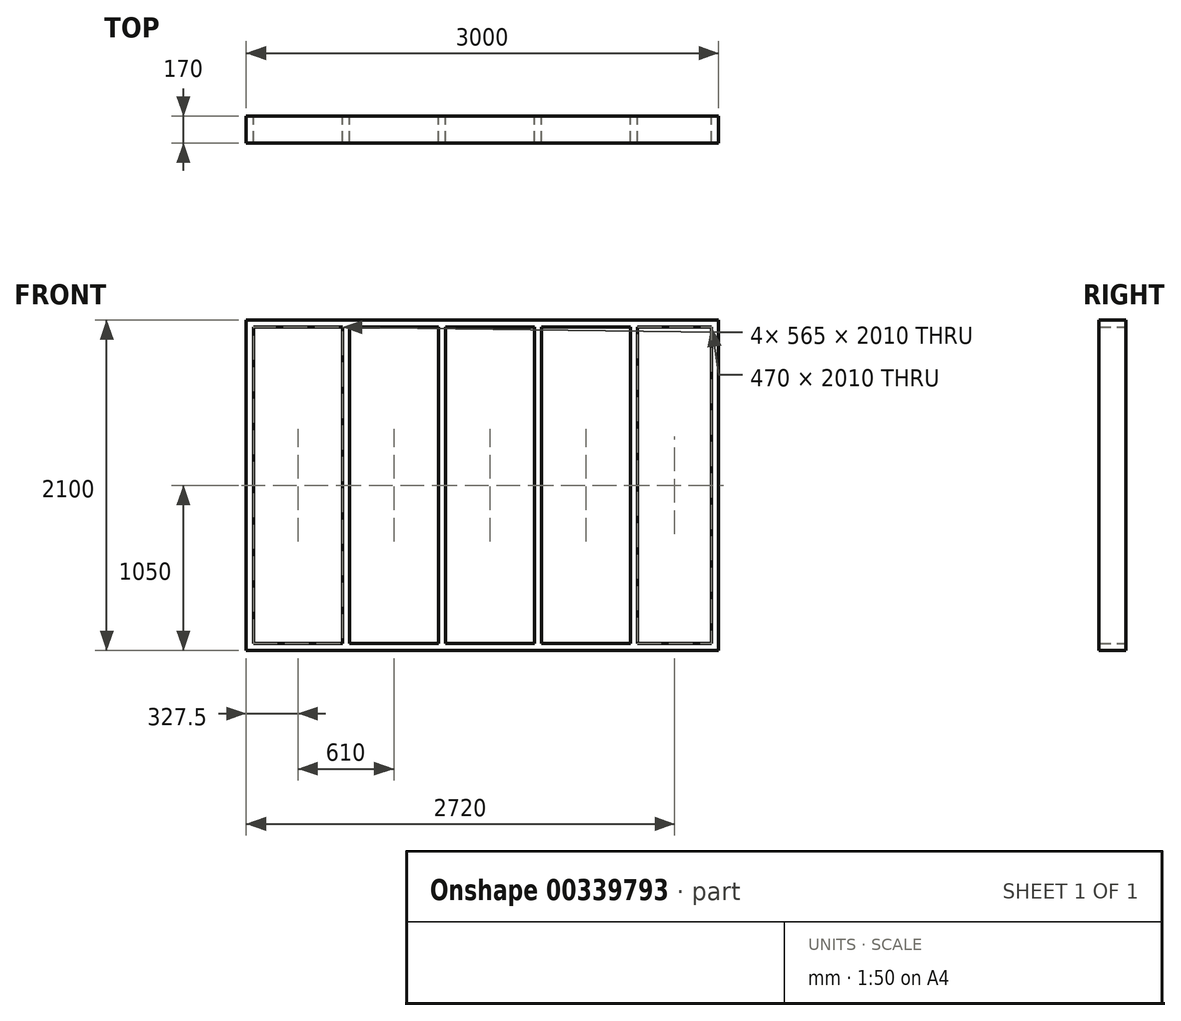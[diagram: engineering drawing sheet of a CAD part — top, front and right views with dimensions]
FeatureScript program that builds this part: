
annotation { "Feature Type Name" : "Feature", "Feature Type Description" : "" }
export const myFeature = defineFeature(function(context is Context, id is Id, definition is map)
    precondition{}
    {
        {
            var Q0;
            Q0=qCreatedBy(makeId("Front.planeOp"),FACE);
            var sketch = newSketch(context, id + "F0", { "sketchPlane" : qUnion([Q0])});
            skLineSegment(sketch, "E0.bottom", {"start": v(0, 0) * mm, "end": v(-3000, 0) * mm});
            skLineSegment(sketch, "E0.top", {"start": v(0, 2100) * mm, "end": v(-3000, 2100) * mm});
            skLineSegment(sketch, "E0.left", {"start": v(0, 0) * mm, "end": v(0, 2100) * mm});
            skLineSegment(sketch, "E0.right", {"start": v(-3000, 0) * mm, "end": v(-3000, 2100) * mm});
            skLineSegment(sketch, "E1.0", {"start": v(-2390, 45) * mm, "end": v(-2390, 2055) * mm});
            skLineSegment(sketch, "E2.0", {"start": v(-1780, 45) * mm, "end": v(-1780, 2055) * mm});
            skLineSegment(sketch, "E3.0", {"start": v(-1170, 45) * mm, "end": v(-1170, 2055) * mm});
            skLineSegment(sketch, "E4.0", {"start": v(-560, 45) * mm, "end": v(-560, 2055) * mm});
            skLineSegment(sketch, "E5.0", {"start": v(-2955, 45) * mm, "end": v(-2955, 2055) * mm});
            skLineSegment(sketch, "E6.0", {"start": v(-2345, 45) * mm, "end": v(-2345, 2055) * mm});
            skLineSegment(sketch, "E7.0", {"start": v(-1735, 45) * mm, "end": v(-1735, 2055) * mm});
            skLineSegment(sketch, "E8.0", {"start": v(-1125, 45) * mm, "end": v(-1125, 2055) * mm});
            skLineSegment(sketch, "E9.0", {"start": v(-515, 45) * mm, "end": v(-515, 2055) * mm});
            skLineSegment(sketch, "E10.0", {"start": v(-45, 2055) * mm, "end": v(-515, 2055) * mm});
            skLineSegment(sketch, "E11.0", {"start": v(-45, 45) * mm, "end": v(-515, 45) * mm});
            skLineSegment(sketch, "E12.trimOffspring", {"start": v(-2390, 2055) * mm, "end": v(-2955, 2055) * mm});
            skLineSegment(sketch, "E13.trimOffspring", {"start": v(-1780, 2055) * mm, "end": v(-2345, 2055) * mm});
            skLineSegment(sketch, "E14.trimOffspring", {"start": v(-1170, 2055) * mm, "end": v(-1735, 2055) * mm});
            skLineSegment(sketch, "E15.trimOffspring", {"start": v(-560, 2055) * mm, "end": v(-1125, 2055) * mm});
            skLineSegment(sketch, "E16.trimOffspring", {"start": v(-560, 45) * mm, "end": v(-1125, 45) * mm});
            skLineSegment(sketch, "E17.trimOffspring", {"start": v(-1170, 45) * mm, "end": v(-1735, 45) * mm});
            skLineSegment(sketch, "E18.trimOffspring", {"start": v(-1780, 45) * mm, "end": v(-2345, 45) * mm});
            skLineSegment(sketch, "E19.trimOffspring", {"start": v(-2390, 45) * mm, "end": v(-2955, 45) * mm});
            skLineSegment(sketch, "E20.0", {"start": v(-45, 45) * mm, "end": v(-45, 2055) * mm});
            skSolve(sketch);
        }
        {
            var Q0;
            Q0=makeQuery(id+"F0.imprint","IMPRINT",FACE,{"disambiguationData":[TD([[makeQuery(id+"F0.imprint","IMPRINT",EDGE,{"derivedFrom":sQuery(id+"F0.wireOp",EDGE,"E0.bottom")}),-1.0]])]});
            extrude(context, id + "F1", {"entities" : qUnion([Q0]), "depth" : 170 * mm});
        }
    });
